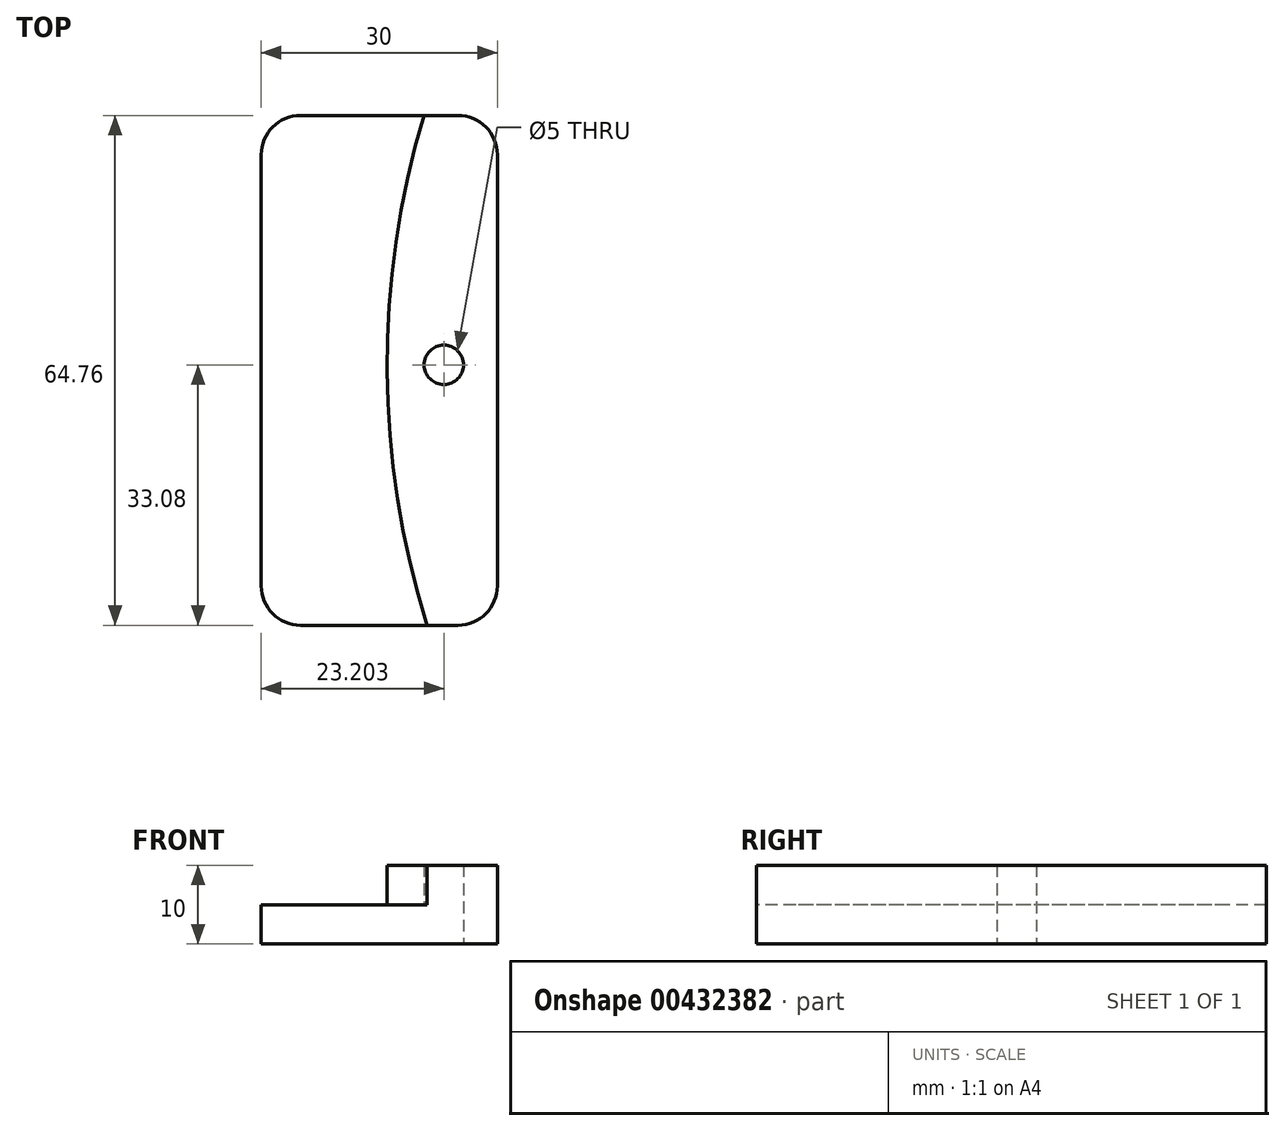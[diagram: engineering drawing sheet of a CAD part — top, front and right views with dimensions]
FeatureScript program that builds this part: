
annotation { "Feature Type Name" : "Feature", "Feature Type Description" : "" }
export const myFeature = defineFeature(function(context is Context, id is Id, definition is map)
    precondition{}
    {
        {
            var Q0;
            Q0=qCreatedBy(makeId("Top.planeOp"),FACE);
            var sketch = newSketch(context, id + "F0", { "sketchPlane" : qUnion([Q0])});
            skCircle(sketch, "E0", {"center": v(0, 0) * mm, "radius": 110 * mm});
            skLineSegment(sketch, "E1", {"start": v(-110, -12.5) * mm, "end": v(-126, -12.5) * mm});
            skLineSegment(sketch, "E2", {"start": v(-126, -12.5) * mm, "end": v(-126, 12.5) * mm});
            skLineSegment(sketch, "E3", {"start": v(-126, 12.5) * mm, "end": v(-110, 12.5) * mm});
            skLineSegment(sketch, "E4.bottom", {"start": v(-126, 31.68) * mm, "end": v(-96, 31.68) * mm});
            skLineSegment(sketch, "E4.top", {"start": v(-126, -33.08) * mm, "end": v(-96, -33.08) * mm});
            skLineSegment(sketch, "E4.left", {"start": v(-126, 31.68) * mm, "end": v(-126, -33.08) * mm});
            skLineSegment(sketch, "E4.right", {"start": v(-96, 31.68) * mm, "end": v(-96, -33.08) * mm});
            skLineSegment(sketch, "E5", {"start": v(-110, 12.5) * mm, "end": v(-109.29, 12.5) * mm});
            skLineSegment(sketch, "E6", {"start": v(-110, -12.5) * mm, "end": v(-109.29, -12.5) * mm});
            skCircle(sketch, "E7", {"center": v(-102.8, 0) * mm, "radius": 2.5 * mm});
            skLineSegment(sketch, "E8", {"start": v(-110, -12.5) * mm, "end": v(-108.75, -12.5) * mm});
            skSolve(sketch);
        }
        {
            var Q0;
            {var subQ0=sQuery(id+"F0.wireOp",EDGE,"E4.right");Q0=makeQuery(id+"F0.imprint","IMPRINT",FACE,{"disambiguationData":[TD([[makeQuery(id+"F0.imprint","IMPRINT",EDGE,{"derivedFrom":subQ0}),-1.0]])]});}
            extrude(context, id + "F1", {"entities" : qUnion([Q0]), "depth" : 10 * mm});
        }
        {
            var Q0;
            {var subQ5=sQuery(id+"F0.wireOp",EDGE,"E3");Q0=makeQuery(id+"F0.imprint","IMPRINT",FACE,{"disambiguationData":[TD([[makeQuery(id+"F0.imprint","IMPRINT",EDGE,{"derivedFrom":subQ5}),1.0]])]});}
            var Q1;
            {var subQ2=sQuery(id+"F0.wireOp",EDGE,"E1");Q1=makeQuery(id+"F0.imprint","IMPRINT",FACE,{"disambiguationData":[TD([[makeQuery(id+"F0.imprint","IMPRINT",EDGE,{"derivedFrom":subQ2}),-1.0]])]});}
            var Q2;
            {var subQ5=sQuery(id+"F0.wireOp",EDGE,"E1");Q2=makeQuery(id+"F0.imprint","IMPRINT",FACE,{"disambiguationData":[TD([[makeQuery(id+"F0.imprint","IMPRINT",EDGE,{"derivedFrom":subQ5}),1.0]])]});}
            extrude(context, id + "F2", {"entities" : qUnion([Q0, Q1, Q2]), "operationType" : NewBodyOperationType.ADD, "depth" : 5 * mm});
        }
        {
            var Q0;
            {var subQ0=sQuery(id+"F0.wireOp",EDGE,"E4.left");var subQ1=sQuery(id+"F0.wireOp",EDGE,"E4.top");Q0=makeQuery(id+"F2.boolean.opBoolean","MERGE",EDGE,{"derivedFrom":[makeQuery(id+"F1.opExtrude","SWEPT_EDGE",EDGE,{"disambiguationData":[OSD([subQ1,subQ0])]}),makeQuery(id+"F2.opExtrude","SWEPT_EDGE",EDGE,{"disambiguationData":[OSD([subQ1,subQ0])]})]});}
            var Q1;
            Q1=makeQuery(id+"F1.opExtrude","SWEPT_EDGE",EDGE,{"disambiguationData":[OSD([sQuery(id+"F0.wireOp",EDGE,"E4.top"),sQuery(id+"F0.wireOp",EDGE,"E4.right")])]});
            var Q2;
            {var subQ0=sQuery(id+"F0.wireOp",EDGE,"E4.left");var subQ1=sQuery(id+"F0.wireOp",EDGE,"E4.bottom");Q2=makeQuery(id+"F2.boolean.opBoolean","MERGE",EDGE,{"derivedFrom":[makeQuery(id+"F1.opExtrude","SWEPT_EDGE",EDGE,{"disambiguationData":[OSD([subQ1,subQ0])]}),makeQuery(id+"F2.opExtrude","SWEPT_EDGE",EDGE,{"disambiguationData":[OSD([subQ1,subQ0])]})]});}
            var Q3;
            Q3=makeQuery(id+"F1.opExtrude","SWEPT_EDGE",EDGE,{"disambiguationData":[OSD([sQuery(id+"F0.wireOp",EDGE,"E4.bottom"),sQuery(id+"F0.wireOp",EDGE,"E4.right")])]});
            var Q4;
            Q4=makeQuery(id+"F2.opExtrude","SWEPT_EDGE",EDGE,{"disambiguationData":[OSD([sQuery(id+"F0.wireOp",EDGE,"E4.top"),sQuery(id+"F0.wireOp",EDGE,"E4.left")])]});
            var Q5;
            Q5=makeQuery(id+"F2.opExtrude","SWEPT_EDGE",EDGE,{"disambiguationData":[OSD([sQuery(id+"F0.wireOp",EDGE,"E4.bottom"),sQuery(id+"F0.wireOp",EDGE,"E4.left")])]});
            fillet(context, id + "F3", {"entities" : qUnion([Q0, Q1, Q2, Q3, Q4, Q5]), "radius" : 5 * mm, "tangentPropagation" : true, "allowEdgeOverflow" : false});
        }
    });
